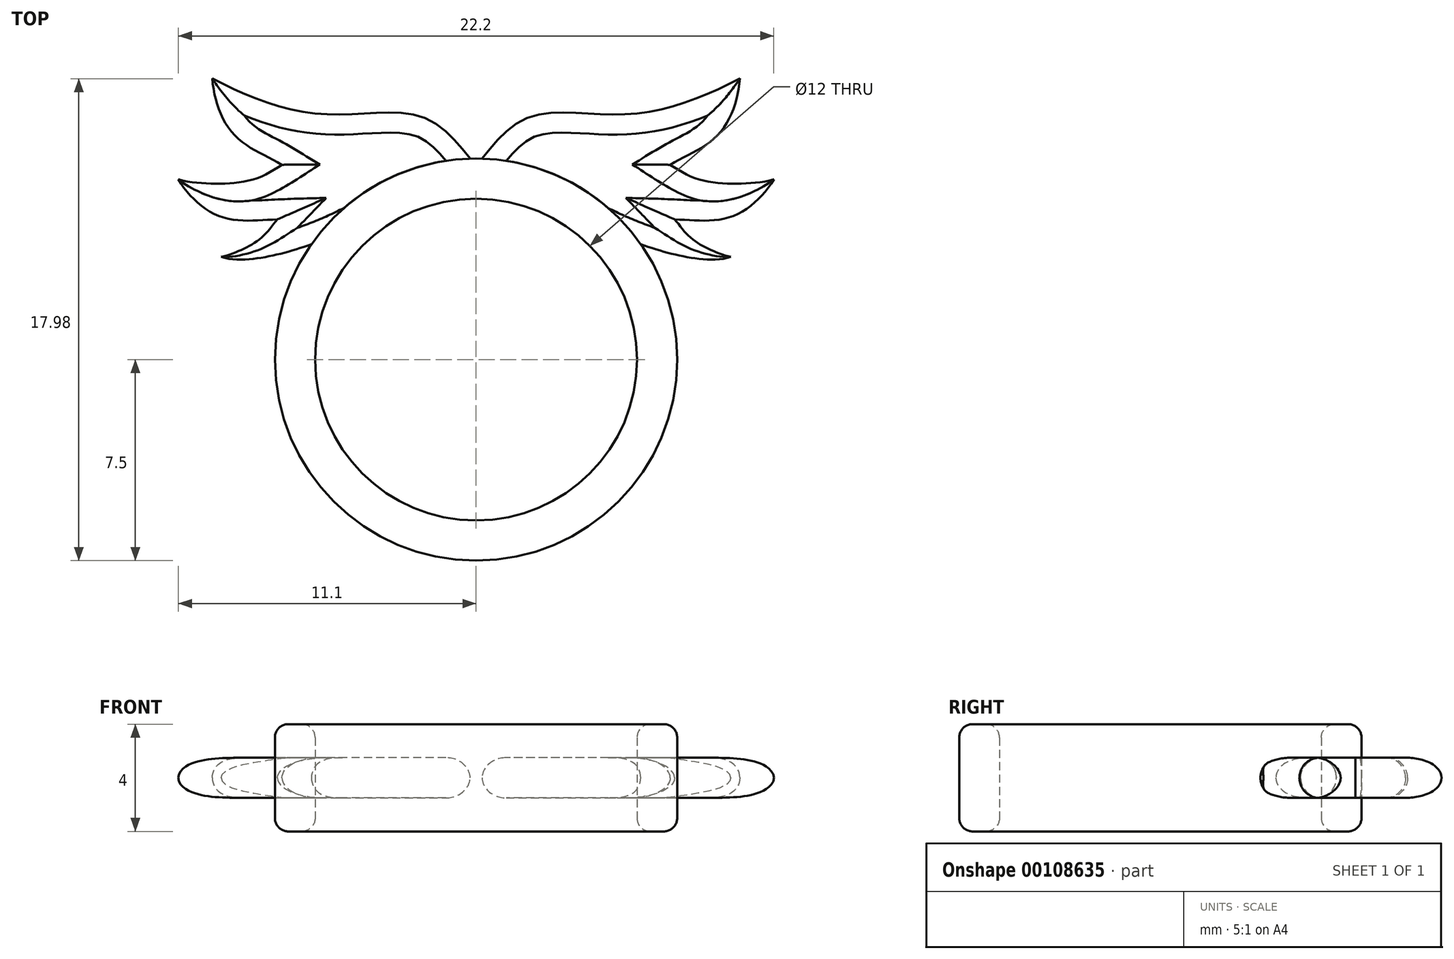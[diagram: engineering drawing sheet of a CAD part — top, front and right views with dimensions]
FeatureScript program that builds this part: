
annotation { "Feature Type Name" : "Feature", "Feature Type Description" : "" }
export const myFeature = defineFeature(function(context is Context, id is Id, definition is map)
    precondition{}
    {
        {
            var Q0;
            Q0=qCreatedBy(makeId("Top.planeOp"),FACE);
            var sketch = newSketch(context, id + "F0", { "sketchPlane" : qUnion([Q0])});
            skCircle(sketch, "E0", {"center": v(0, 0) * mm, "radius": 6 * mm});
            skCircle(sketch, "E1", {"center": v(0, 0) * mm, "radius": 7.5 * mm});
            skPoint(sketch, "E2", {"position": v(-4.26, 9.97) * mm});
            skPoint(sketch, "E3.MirrorP", {"position": v(4.26, 9.97) * mm});
            skSolve(sketch);
        }
        {
            var Q0;
            Q0=qSketchRegion(id+"F0",true);
            extrude(context, id + "F1", {"entities" : qUnion([Q0]), "endBound" : BoundingType.SYMMETRIC, "depth" : 4 * mm});
        }
        {
            var Q0;
            Q0=makeQuery(id+"F1.opExtrude","CAP_EDGE",EDGE,{"disambiguationData":[OSD([sQuery(id+"F0.wireOp",EDGE,"E0")])],"isStart":true});
            var Q1;
            Q1=makeQuery(id+"F1.opExtrude","CAP_EDGE",EDGE,{"disambiguationData":[OSD([sQuery(id+"F0.wireOp",EDGE,"E0")])],"isStart":false});
            var Q2;
            Q2=makeQuery(id+"F1.opExtrude","CAP_EDGE",EDGE,{"disambiguationData":[OSD([sQuery(id+"F0.wireOp",EDGE,"E1")])],"isStart":false});
            var Q3;
            Q3=makeQuery(id+"F1.opExtrude","CAP_EDGE",EDGE,{"disambiguationData":[OSD([sQuery(id+"F0.wireOp",EDGE,"E1")])],"isStart":true});
            fillet(context, id + "F2", {"entities" : qUnion([Q0, Q1, Q2, Q3]), "radius" : 0.5 * mm, "tangentPropagation" : true, "allowEdgeOverflow" : false});
        }
        {
            var Q0;
            Q0=makeQuery(id+"F0.imprint","IMPRINT",FACE,{"disambiguationData":[TD([[makeQuery(id+"F0.imprint","IMPRINT",EDGE,{"derivedFrom":sQuery(id+"F0.wireOp",EDGE,"E0")}),1.0]])]});
            extrude(context, id + "F3", {"entities" : qUnion([Q0]), "operationType" : NewBodyOperationType.REMOVE, "endBound" : BoundingType.SYMMETRIC, "oppositeDirection" : true, "depth" : 5 * mm});
        }
        {
            var Q0;
            Q0=qCreatedBy(makeId("Top.planeOp"),FACE);
            var sketch = newSketch(context, id + "F4", { "sketchPlane" : qUnion([Q0])});
            skFitSpline(sketch, "E4", {"points": [v(0, 7.22) * mm, v(1.93, 9.03) * mm, v(5.92, 9.17) * mm, v(9.84, 10.48) * mm], "startDerivative": vector(5.34, 6.32) * mm, "endDerivative": vector(8.05, 4.12) * mm});
            skFitSpline(sketch, "E5", {"points": [v(9.84, 10.48) * mm, v(9.1, 8.48) * mm, v(7.24, 7.27) * mm], "startDerivative": vector(-0.3, -3.2) * mm, "endDerivative": vector(-2.48, -1.53) * mm});
            skFitSpline(sketch, "E6", {"points": [v(7.24, 7.27) * mm, v(8.55, 6.66) * mm, v(11.1, 6.72) * mm], "startDerivative": vector(2.58, -1.64) * mm, "endDerivative": vector(3, 0.87) * mm});
            skFitSpline(sketch, "E7", {"points": [v(11.1, 6.72) * mm, v(9.52, 5.33) * mm, v(7.4, 5.23) * mm], "startDerivative": vector(-2.04, -3.35) * mm, "endDerivative": vector(-3.68, 0.1) * mm});
            skFitSpline(sketch, "E8", {"points": [v(7.4, 5.23) * mm, v(8.04, 4.5) * mm, v(9.5, 3.84) * mm], "startDerivative": vector(1.6, -1.65) * mm, "endDerivative": vector(2, -0.32) * mm});
            skFitSpline(sketch, "E9", {"points": [v(9.5, 3.84) * mm, v(7.37, 3.93) * mm, v(4.7, 4.93) * mm], "startDerivative": vector(-3.5, -1.28) * mm, "endDerivative": vector(-4.95, 2.46) * mm});
            skLineSegment(sketch, "E10", {"start": v(0, 7.22) * mm, "end": v(4.7, 4.93) * mm});
            skFitSpline(sketch, "E11.MirrorCS", {"points": [v(-7.4, 5.23) * mm, v(-8.04, 4.5) * mm, v(-9.5, 3.84) * mm], "startDerivative": vector(-1.6, -1.65) * mm, "endDerivative": vector(-2, -0.32) * mm});
            skFitSpline(sketch, "E12.MirrorCS", {"points": [v(-9.84, 10.48) * mm, v(-9.1, 8.48) * mm, v(-7.24, 7.27) * mm], "startDerivative": vector(0.3, -3.2) * mm, "endDerivative": vector(2.48, -1.53) * mm});
            skFitSpline(sketch, "E13.MirrorCS", {"points": [v(0, 7.22) * mm, v(-1.93, 9.03) * mm, v(-5.92, 9.17) * mm, v(-9.84, 10.48) * mm], "startDerivative": vector(-5.34, 6.32) * mm, "endDerivative": vector(-8.05, 4.12) * mm});
            skFitSpline(sketch, "E14.MirrorCS", {"points": [v(-7.24, 7.27) * mm, v(-8.55, 6.66) * mm, v(-11.1, 6.72) * mm], "startDerivative": vector(-2.58, -1.64) * mm, "endDerivative": vector(-3, 0.87) * mm});
            skFitSpline(sketch, "E15.MirrorCS", {"points": [v(-11.1, 6.72) * mm, v(-9.52, 5.33) * mm, v(-7.4, 5.23) * mm], "startDerivative": vector(2.04, -3.35) * mm, "endDerivative": vector(3.68, 0.1) * mm});
            skFitSpline(sketch, "E16.MirrorCS", {"points": [v(-9.5, 3.84) * mm, v(-7.37, 3.93) * mm, v(-4.7, 4.93) * mm], "startDerivative": vector(3.5, -1.28) * mm, "endDerivative": vector(4.95, 2.46) * mm});
            skLineSegment(sketch, "E17.MirrorCS", {"start": v(0, 7.22) * mm, "end": v(-4.7, 4.93) * mm});
            skSolve(sketch);
        }
        {
            var Q0;
            Q0 = qSketchRegion(id + "F4", true);
            extrude(context, id + "F5", {"entities" : qUnion([Q0]), "operationType" : NewBodyOperationType.ADD, "endBound" : BoundingType.SYMMETRIC, "depth" : 1.5 * mm});
        }
        {
            var Q0;
            Q0=makeQuery(id+"F5.opExtrude","CAP_EDGE",EDGE,{"disambiguationData":[OSD([sQuery(id+"F4.wireOp",EDGE,"E4")])],"isStart":false});
            var Q1;
            Q1=makeQuery(id+"F5.opExtrude","CAP_EDGE",EDGE,{"disambiguationData":[OSD([sQuery(id+"F4.wireOp",EDGE,"E13.MirrorCS")])],"isStart":true});
            var Q2;
            Q2=makeQuery(id+"F5.opExtrude","CAP_EDGE",EDGE,{"disambiguationData":[OSD([sQuery(id+"F4.wireOp",EDGE,"E13.MirrorCS")])],"isStart":false});
            var Q3;
            Q3=makeQuery(id+"F5.opExtrude","CAP_EDGE",EDGE,{"disambiguationData":[OSD([sQuery(id+"F4.wireOp",EDGE,"E4")])],"isStart":true});
            var Q4;
            Q4=makeQuery(id+"F5.opExtrude","CAP_EDGE",EDGE,{"disambiguationData":[OSD([sQuery(id+"F4.wireOp",EDGE,"E5")])],"isStart":false});
            var Q5;
            Q5=makeQuery(id+"F5.opExtrude","CAP_EDGE",EDGE,{"disambiguationData":[OSD([sQuery(id+"F4.wireOp",EDGE,"E6")])],"isStart":false});
            var Q6;
            Q6=makeQuery(id+"F5.opExtrude","CAP_EDGE",EDGE,{"disambiguationData":[OSD([sQuery(id+"F4.wireOp",EDGE,"E7")])],"isStart":false});
            var Q7;
            Q7=makeQuery(id+"F5.opExtrude","CAP_EDGE",EDGE,{"disambiguationData":[OSD([sQuery(id+"F4.wireOp",EDGE,"E8")])],"isStart":false});
            var Q8;
            Q8=makeQuery(id+"F5.opExtrude","CAP_EDGE",EDGE,{"disambiguationData":[OSD([sQuery(id+"F4.wireOp",EDGE,"E9")])],"isStart":false});
            var Q9;
            Q9=makeQuery(id+"F5.opExtrude","CAP_EDGE",EDGE,{"disambiguationData":[OSD([sQuery(id+"F4.wireOp",EDGE,"E9")])],"isStart":true});
            var Q10;
            Q10=makeQuery(id+"F5.opExtrude","CAP_EDGE",EDGE,{"disambiguationData":[OSD([sQuery(id+"F4.wireOp",EDGE,"E7")])],"isStart":true});
            var Q11;
            Q11=makeQuery(id+"F5.opExtrude","CAP_EDGE",EDGE,{"disambiguationData":[OSD([sQuery(id+"F4.wireOp",EDGE,"E8")])],"isStart":true});
            var Q12;
            Q12=makeQuery(id+"F5.opExtrude","CAP_EDGE",EDGE,{"disambiguationData":[OSD([sQuery(id+"F4.wireOp",EDGE,"E6")])],"isStart":true});
            var Q13;
            Q13=makeQuery(id+"F5.opExtrude","CAP_EDGE",EDGE,{"disambiguationData":[OSD([sQuery(id+"F4.wireOp",EDGE,"E5")])],"isStart":true});
            var Q14;
            Q14=makeQuery(id+"F5.opExtrude","CAP_EDGE",EDGE,{"disambiguationData":[OSD([sQuery(id+"F4.wireOp",EDGE,"E12.MirrorCS")])],"isStart":true});
            var Q15;
            Q15=makeQuery(id+"F5.opExtrude","CAP_EDGE",EDGE,{"disambiguationData":[OSD([sQuery(id+"F4.wireOp",EDGE,"E14.MirrorCS")])],"isStart":true});
            var Q16;
            Q16=makeQuery(id+"F5.opExtrude","CAP_EDGE",EDGE,{"disambiguationData":[OSD([sQuery(id+"F4.wireOp",EDGE,"E15.MirrorCS")])],"isStart":true});
            var Q17;
            Q17=makeQuery(id+"F5.opExtrude","CAP_EDGE",EDGE,{"disambiguationData":[OSD([sQuery(id+"F4.wireOp",EDGE,"E11.MirrorCS")])],"isStart":true});
            var Q18;
            Q18=makeQuery(id+"F5.opExtrude","CAP_EDGE",EDGE,{"disambiguationData":[OSD([sQuery(id+"F4.wireOp",EDGE,"E16.MirrorCS")])],"isStart":true});
            var Q19;
            Q19=makeQuery(id+"F5.opExtrude","CAP_EDGE",EDGE,{"disambiguationData":[OSD([sQuery(id+"F4.wireOp",EDGE,"E12.MirrorCS")])],"isStart":false});
            var Q20;
            Q20=makeQuery(id+"F5.opExtrude","CAP_EDGE",EDGE,{"disambiguationData":[OSD([sQuery(id+"F4.wireOp",EDGE,"E14.MirrorCS")])],"isStart":false});
            var Q21;
            Q21=makeQuery(id+"F5.opExtrude","CAP_EDGE",EDGE,{"disambiguationData":[OSD([sQuery(id+"F4.wireOp",EDGE,"E15.MirrorCS")])],"isStart":false});
            var Q22;
            Q22=makeQuery(id+"F5.opExtrude","CAP_EDGE",EDGE,{"disambiguationData":[OSD([sQuery(id+"F4.wireOp",EDGE,"E11.MirrorCS")])],"isStart":false});
            var Q23;
            Q23=makeQuery(id+"F5.opExtrude","CAP_EDGE",EDGE,{"disambiguationData":[OSD([sQuery(id+"F4.wireOp",EDGE,"E16.MirrorCS")])],"isStart":false});
            fillet(context, id + "F6", {"entities" : qUnion([Q0, Q1, Q2, Q3, Q4, Q5, Q6, Q7, Q8, Q9, Q10, Q11, Q12, Q13, Q14, Q15, Q16, Q17, Q18, Q19, Q20, Q21, Q22, Q23]), "radius" : 0.75 * mm, "tangentPropagation" : true, "allowEdgeOverflow" : false});
        }
    });
